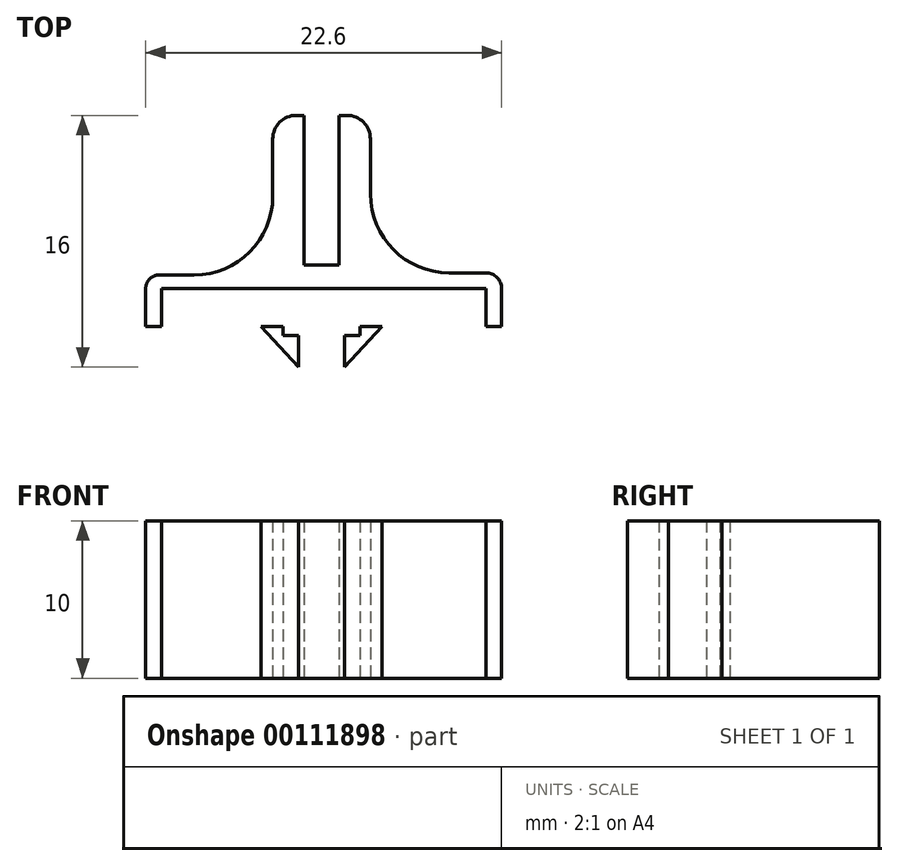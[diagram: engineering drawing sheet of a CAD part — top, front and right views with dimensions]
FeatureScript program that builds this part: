
annotation { "Feature Type Name" : "Feature", "Feature Type Description" : "" }
export const myFeature = defineFeature(function(context is Context, id is Id, definition is map)
    precondition{}
    {
        {
            var Q0;
            Q0=qCreatedBy(makeId("Top.planeOp"),FACE);
            var sketch = newSketch(context, id + "F0", { "sketchPlane" : qUnion([Q0])});
            skLineSegment(sketch, "E0.bottom", {"start": v(-10.17, -5.5) * mm, "end": v(10.43, -5.5) * mm});
            skLineSegment(sketch, "E0.top", {"start": v(-10.17, -4.64) * mm, "end": v(-8.1, -4.64) * mm});
            skLineSegment(sketch, "E0.left", {"start": v(-10.17, -5.5) * mm, "end": v(-10.17, -4.64) * mm});
            skLineSegment(sketch, "E0.right", {"start": v(10.43, -5.5) * mm, "end": v(10.43, -4.5) * mm});
            skLineSegment(sketch, "E1.bottom", {"start": v(10.43, -5.5) * mm, "end": v(11.43, -5.5) * mm});
            skLineSegment(sketch, "E1.top", {"start": v(10.43, -7.9) * mm, "end": v(11.43, -7.9) * mm});
            skLineSegment(sketch, "E1.left", {"start": v(10.43, -5.5) * mm, "end": v(10.43, -7.9) * mm});
            skLineSegment(sketch, "E1.right", {"start": v(11.43, -5.5) * mm, "end": v(11.43, -7.9) * mm});
            skArc(sketch, "E2", {"start": v(11.43, -5.5) * mm, "mid": v(11.14, -4.8) * mm, "end": v(10.43, -4.5) * mm});
            skLineSegment(sketch, "E3.bottom", {"start": v(-10.17, -5.5) * mm, "end": v(-11.17, -5.5) * mm});
            skLineSegment(sketch, "E3.top", {"start": v(-10.17, -7.9) * mm, "end": v(-11.17, -7.9) * mm});
            skLineSegment(sketch, "E3.left", {"start": v(-10.17, -5.5) * mm, "end": v(-10.17, -7.9) * mm});
            skLineSegment(sketch, "E3.right", {"start": v(-11.17, -5.5) * mm, "end": v(-11.17, -7.9) * mm});
            skArc(sketch, "E4", {"start": v(-10.17, -4.64) * mm, "mid": v(-10.87, -4.84) * mm, "end": v(-11.17, -5.5) * mm});
            skLineSegment(sketch, "E5", {"start": v(-2.45, -5.5) * mm, "end": v(2.45, -5.5) * mm, "construction": true});
            skLineSegment(sketch, "E6.bottom", {"start": v(-2.45, -5.5) * mm, "end": v(-1.45, -5.5) * mm});
            skLineSegment(sketch, "E6.top", {"start": v(-2.45, -8.5) * mm, "end": v(-1.45, -8.5) * mm});
            skLineSegment(sketch, "E6.left", {"start": v(-2.45, -5.5) * mm, "end": v(-2.45, -8.5) * mm});
            skLineSegment(sketch, "E6.right", {"start": v(-1.45, -5.5) * mm, "end": v(-1.45, -8.5) * mm});
            skLineSegment(sketch, "E7.bottom", {"start": v(2.45, -5.5) * mm, "end": v(1.45, -5.5) * mm});
            skLineSegment(sketch, "E7.top", {"start": v(2.45, -8.5) * mm, "end": v(1.45, -8.5) * mm});
            skLineSegment(sketch, "E7.left", {"start": v(2.45, -5.5) * mm, "end": v(2.45, -8.5) * mm});
            skLineSegment(sketch, "E7.right", {"start": v(1.45, -5.5) * mm, "end": v(1.45, -8.5) * mm});
            skLineSegment(sketch, "E8", {"start": v(3.85, -7.9) * mm, "end": v(2.45, -7.9) * mm});
            skLineSegment(sketch, "E9", {"start": v(-2.45, -7.9) * mm, "end": v(-3.85, -7.9) * mm});
            skLineSegment(sketch, "E10", {"start": v(-2.45, -7.9) * mm, "end": v(2.45, -7.9) * mm, "construction": true});
            skLineSegment(sketch, "E11", {"start": v(1.45, -8.5) * mm, "end": v(1.45, -10.5) * mm});
            skLineSegment(sketch, "E12", {"start": v(1.45, -10.5) * mm, "end": v(3.85, -7.9) * mm});
            skLineSegment(sketch, "E13", {"start": v(-1.45, -8.5) * mm, "end": v(-1.45, -10.5) * mm});
            skLineSegment(sketch, "E14", {"start": v(-1.45, -10.5) * mm, "end": v(-3.85, -7.9) * mm});
            skLineSegment(sketch, "E15", {"start": v(-1.1, -4) * mm, "end": v(1.1, -4) * mm});
            skLineSegment(sketch, "E16", {"start": v(8.1, -4.5) * mm, "end": v(10.43, -4.5) * mm});
            skLineSegment(sketch, "E17", {"start": v(-3.1, 0.36) * mm, "end": v(-3.1, 4) * mm});
            skLineSegment(sketch, "E18", {"start": v(-1.1, -4) * mm, "end": v(-1.1, 5.5) * mm});
            skLineSegment(sketch, "E19", {"start": v(-1.1, 5.5) * mm, "end": v(-1.6, 5.5) * mm});
            skLineSegment(sketch, "E20", {"start": v(1.1, -4) * mm, "end": v(1.1, 5.5) * mm});
            skLineSegment(sketch, "E21", {"start": v(3.1, 0.5) * mm, "end": v(3.1, 4) * mm});
            skLineSegment(sketch, "E22", {"start": v(1.6, 5.5) * mm, "end": v(1.1, 5.5) * mm});
            skLineSegment(sketch, "E23", {"start": v(-1.1, 5.5) * mm, "end": v(1.1, 5.5) * mm, "construction": true});
            skPoint(sketch, "E24", {"position": v(0, 5.5) * mm});
            skPoint(sketch, "E25.visualSharp", {"position": v(-3.1, -4.64) * mm});
            skArc(sketch, "E25.filletArc", {"start": v(-8.1, -4.64) * mm, "mid": v(-4.56, -3.18) * mm, "end": v(-3.1, 0.36) * mm});
            skPoint(sketch, "E26.visualSharp", {"position": v(3.1, -4.5) * mm});
            skArc(sketch, "E26.filletArc", {"start": v(3.1, 0.5) * mm, "mid": v(4.56, -3.04) * mm, "end": v(8.1, -4.5) * mm});
            skPoint(sketch, "E27.visualSharp", {"position": v(-3.1, 5.5) * mm});
            skArc(sketch, "E27.filletArc", {"start": v(-1.6, 5.5) * mm, "mid": v(-2.66, 5.06) * mm, "end": v(-3.1, 4) * mm});
            skPoint(sketch, "E28.visualSharp", {"position": v(3.1, 5.5) * mm});
            skArc(sketch, "E28.filletArc", {"start": v(3.1, 4) * mm, "mid": v(2.66, 5.06) * mm, "end": v(1.6, 5.5) * mm});
            skPoint(sketch, "E29", {"position": v(0, -7.9) * mm});
            skSolve(sketch);
        }
        {
            var Q0;
            Q0=makeQuery(id+"F0.imprint","IMPRINT",FACE,{"disambiguationData":[TD([[makeQuery(id+"F0.imprint","IMPRINT",EDGE,{"derivedFrom":sQuery(id+"F0.wireOp",EDGE,"E1.bottom")}),-1.0]])]});
            var Q1;
            Q1=makeQuery(id+"F0.imprint","IMPRINT",FACE,{"disambiguationData":[TD([[makeQuery(id+"F0.imprint","IMPRINT",EDGE,{"derivedFrom":sQuery(id+"F0.wireOp",EDGE,"E3.bottom")}),1.0]])]});
            var Q2;
            {var subQ1=sQuery(id+"F0.wireOp",EDGE,"E9");Q2=makeQuery(id+"F0.imprint","IMPRINT",FACE,{"disambiguationData":[TD([[makeQuery(id+"F0.imprint","IMPRINT",EDGE,{"derivedFrom":subQ1}),1.0]])]});}
            var Q3;
            {var subQ1=sQuery(id+"F0.wireOp",EDGE,"7c9eb7b9-ca48-4d36-bab2-391d59fa54ff");Q3=makeQuery(id+"F0.imprint","IMPRINT",FACE,{"disambiguationData":[TD([[makeQuery(id+"F0.imprint","IMPRINT",EDGE,{"derivedFrom":subQ1}),-1.0]])]});}
            var Q4;
            Q4=makeQuery(id+"F0.imprint","IMPRINT",FACE,{"disambiguationData":[TD([[makeQuery(id+"F0.imprint","IMPRINT",EDGE,{"derivedFrom":sQuery(id+"F0.wireOp",EDGE,"E0.left")}),1.0]])]});
            var Q5;
            Q5=makeQuery(id+"F0.imprint","IMPRINT",FACE,{"disambiguationData":[TD([[makeQuery(id+"F0.imprint","IMPRINT",EDGE,{"derivedFrom":sQuery(id+"F0.wireOp",EDGE,"E0.right")}),-1.0]])]});
            var Q6;
            {var subQ3=sQuery(id+"F0.wireOp",EDGE,"E6.bottom");Q6=makeQuery(id+"F0.imprint","IMPRINT",FACE,{"disambiguationData":[TD([[makeQuery(id+"F0.imprint","IMPRINT",EDGE,{"derivedFrom":subQ3}),-1.0]])]});}
            var Q7;
            {var subQ2=sQuery(id+"F0.wireOp",EDGE,"E7.bottom");Q7=makeQuery(id+"F0.imprint","IMPRINT",FACE,{"disambiguationData":[TD([[makeQuery(id+"F0.imprint","IMPRINT",EDGE,{"derivedFrom":subQ2}),1.0]])]});}
            var Q8;
            {var subQ0=sQuery(id+"F0.wireOp",EDGE,"7cf5e282-fc27-4f11-9d7e-3bad8ab92ec3");Q8=makeQuery(id+"F0.imprint","IMPRINT",FACE,{"disambiguationData":[TD([[makeQuery(id+"F0.imprint","IMPRINT",EDGE,{"derivedFrom":subQ0}),1.0]])]});}
            var Q9;
            {var subQ0=sQuery(id+"F0.wireOp",EDGE,"9b068b05-5ba9-4f17-919f-f73491ae4f90");Q9=makeQuery(id+"F0.imprint","IMPRINT",FACE,{"disambiguationData":[TD([[makeQuery(id+"F0.imprint","IMPRINT",EDGE,{"derivedFrom":subQ0}),-1.0]])]});}
            var Q10;
            {var subQ1=sQuery(id+"F0.wireOp",EDGE,"E0.left");Q10=makeQuery(id+"F0.imprint","IMPRINT",FACE,{"disambiguationData":[TD([[makeQuery(id+"F0.imprint","IMPRINT",EDGE,{"derivedFrom":subQ1}),-1.0]])]});}
            var Q11;
            {var subQ1=sQuery(id+"F0.wireOp",EDGE,"E0.right");Q11=makeQuery(id+"F0.imprint","IMPRINT",FACE,{"disambiguationData":[TD([[makeQuery(id+"F0.imprint","IMPRINT",EDGE,{"derivedFrom":subQ1}),1.0]])]});}
            var Q12;
            {var subQ0=sQuery(id+"F0.wireOp",EDGE,"E0.top");var subQ2=sQuery(id+"F0.wireOp",EDGE,"ccbefe15-ddc9-4d3c-9180-5a0c61267b28");var subQ4=makeQuery(id+"F0.imprint","INTERSECT",VERTEX,{"disambiguationData":[OD(0.0)],"derivedFrom":[subQ2,subQ0]});Q12=makeQuery(id+"F0.imprint","IMPRINT",FACE,{"disambiguationData":[TD([[makeQuery(id+"F0.imprint","IMPRINT",EDGE,{"disambiguationData":[TD([[subQ4,-1.0]])],"derivedFrom":subQ2}),1.0]])]});}
            var Q13;
            {var subQ2=sQuery(id+"F0.wireOp",EDGE,"E7.top");Q13=makeQuery(id+"F0.imprint","IMPRINT",FACE,{"disambiguationData":[TD([[makeQuery(id+"F0.imprint","IMPRINT",EDGE,{"derivedFrom":subQ2}),1.0]])]});}
            extrude(context, id + "F1", {"entities" : qUnion([Q0, Q1, Q2, Q3, Q4, Q5, Q6, Q7, Q8, Q9, Q10, Q11, Q12, Q13]), "depth" : 10 * mm});
        }
    });
